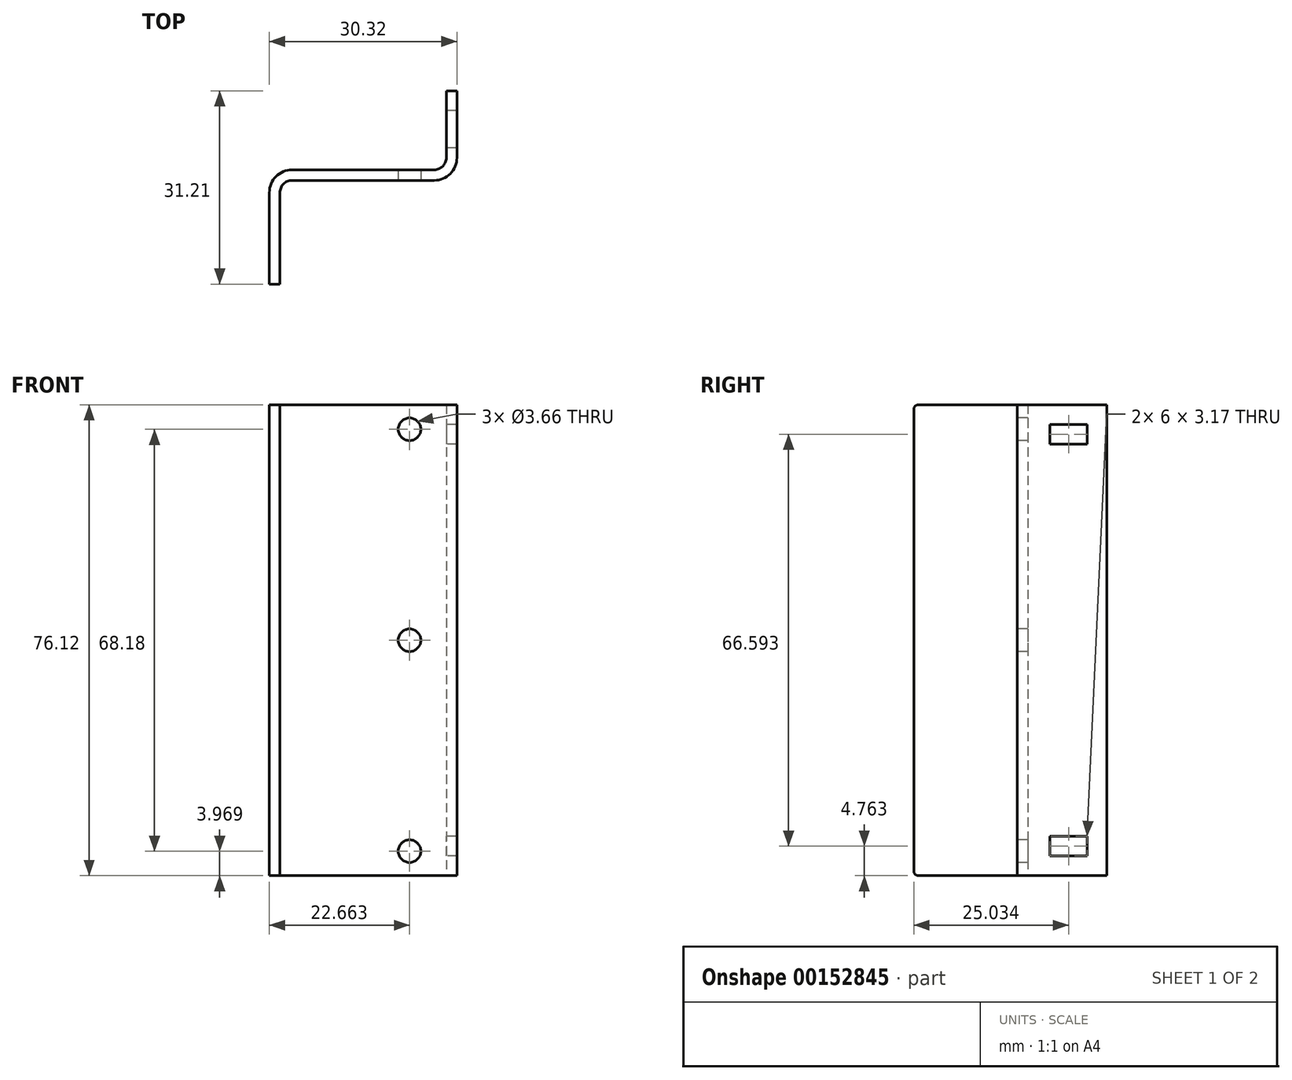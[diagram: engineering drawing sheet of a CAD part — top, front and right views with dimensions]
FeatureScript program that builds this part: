
annotation { "Feature Type Name" : "Feature", "Feature Type Description" : "" }
export const myFeature = defineFeature(function(context is Context, id is Id, definition is map)
    precondition{}
    {
        {
            var Q0;
            Q0=qCreatedBy(makeId("Top.planeOp"),FACE);
            var sketch = newSketch(context, id + "F0", { "sketchPlane" : qUnion([Q0])});
            skLineSegment(sketch, "E0.bottom", {"start": v(0, 0) * mm, "end": v(-1.7, 0) * mm});
            skLineSegment(sketch, "E1.left", {"start": v(0, 0) * mm, "end": v(0, 16.75) * mm});
            skLineSegment(sketch, "E1.right", {"start": v(-1.7, 0) * mm, "end": v(-1.7, 18.46) * mm});
            skLineSegment(sketch, "E2.bottom", {"start": v(0, 16.75) * mm, "end": v(28.61, 16.75) * mm});
            skLineSegment(sketch, "E2.top", {"start": v(-1.7, 18.46) * mm, "end": v(26.9, 18.46) * mm});
            skLineSegment(sketch, "E3", {"start": v(0, 16.75) * mm, "end": v(-1.7, 16.75) * mm, "construction": true});
            skLineSegment(sketch, "E4", {"start": v(0, 16.75) * mm, "end": v(0, 18.46) * mm, "construction": true});
            skLineSegment(sketch, "E5", {"start": v(28.61, 16.75) * mm, "end": v(28.61, 31.2) * mm});
            skLineSegment(sketch, "E6", {"start": v(28.61, 31.2) * mm, "end": v(26.9, 31.2) * mm});
            skLineSegment(sketch, "E7", {"start": v(26.9, 31.2) * mm, "end": v(26.9, 18.46) * mm});
            skSolve(sketch);
        }
        {
            var Q0;
            Q0=qSketchRegion(id+"F0",true);
            extrude(context, id + "F1", {"entities" : qUnion([Q0]), "depth" : 76.12 * mm});
        }
        {
            var Q0;
            Q0=makeQuery(id+"F1.opExtrude","SWEPT_EDGE",EDGE,{"disambiguationData":[OSD([sQuery(id+"F0.wireOp",EDGE,"E1.left"),sQuery(id+"F0.wireOp",EDGE,"E2.bottom")])]});
            var Q1;
            Q1=makeQuery(id+"F1.opExtrude","SWEPT_EDGE",EDGE,{"disambiguationData":[OSD([sQuery(id+"F0.wireOp",EDGE,"E1.left"),sQuery(id+"F0.wireOp",EDGE,"E2.bottom")])]});
            var Q2;
            Q2=makeQuery(id+"F1.opExtrude","SWEPT_EDGE",EDGE,{"disambiguationData":[OSD([sQuery(id+"F0.wireOp",EDGE,"E2.top"),sQuery(id+"F0.wireOp",EDGE,"E7")])]});
            fillet(context, id + "F2", {"entities" : qUnion([Q0, Q1, Q2]), "radius" : 1.98 * mm, "tangentPropagation" : true, "allowEdgeOverflow" : false});
        }
        {
            var Q0;
            Q0=makeQuery(id+"F1.opExtrude","SWEPT_EDGE",EDGE,{"disambiguationData":[OSD([sQuery(id+"F0.wireOp",EDGE,"E1.right"),sQuery(id+"F0.wireOp",EDGE,"E2.top")])]});
            var Q1;
            Q1=makeQuery(id+"F1.opExtrude","SWEPT_EDGE",EDGE,{"disambiguationData":[OSD([sQuery(id+"F0.wireOp",EDGE,"E1.right"),sQuery(id+"F0.wireOp",EDGE,"E2.top")])]});
            var Q2;
            Q2=makeQuery(id+"F1.opExtrude","SWEPT_EDGE",EDGE,{"disambiguationData":[OSD([sQuery(id+"F0.wireOp",EDGE,"E2.bottom"),sQuery(id+"F0.wireOp",EDGE,"E5")])]});
            fillet(context, id + "F3", {"entities" : qUnion([Q0, Q1, Q2]), "radius" : 3.7 * mm, "tangentPropagation" : true, "allowEdgeOverflow" : false});
        }
        {
            var Q0;
            Q0=makeQuery(id+"F1.opExtrude","SWEPT_FACE",FACE,{"disambiguationData":[OSD([sQuery(id+"F0.wireOp",EDGE,"E2.bottom")])]});
            var sketch = newSketch(context, id + "F4", { "sketchPlane" : qUnion([Q0])});
            skLineSegment(sketch, "E8", {"start": v(20.95, 76.12) * mm, "end": v(20.95, 72.15) * mm, "construction": true});
            skLineSegment(sketch, "E9", {"start": v(20.95, 72.15) * mm, "end": v(20.95, 3.97) * mm, "construction": true});
            skLineSegment(sketch, "E10", {"start": v(20.95, 3.97) * mm, "end": v(20.95, 0) * mm, "construction": true});
            skLineSegment(sketch, "E11", {"start": v(20.95, 38.06) * mm, "end": v(24.92, 38.06) * mm, "construction": true});
            skCircle(sketch, "E12", {"center": v(20.95, 72.15) * mm, "radius": 1.83 * mm});
            skCircle(sketch, "E13", {"center": v(20.95, 38.06) * mm, "radius": 1.83 * mm});
            skCircle(sketch, "E14", {"center": v(20.95, 3.97) * mm, "radius": 1.83 * mm});
            skSolve(sketch);
        }
        {
            var Q0;
            Q0 = qSketchRegion(id + "F4", true);
            var Q1;
            Q1=makeQuery(id+"F1.opExtrude","SWEPT_FACE",FACE,{"disambiguationData":[OSD([sQuery(id+"F0.wireOp",EDGE,"E2.top")])]});
            extrude(context, id + "F5", {"entities" : qUnion([Q0]), "operationType" : NewBodyOperationType.REMOVE, "endBound" : BoundingType.UP_TO_SURFACE, "oppositeDirection" : true, "endBoundEntityFace" : qUnion([Q1]), "depth" : 25.4 * mm});
        }
        {
            var Q0;
            Q0=makeQuery(id+"F1.opExtrude","CAP_EDGE",EDGE,{"disambiguationData":[OSD([sQuery(id+"F0.wireOp",EDGE,"CBXVxerA-JZwe-1R4C-h2t0-RdQutqAmHxP0")])],"isStart":false});
            var Q1;
            Q1=makeQuery(id+"F1.opExtrude","CAP_EDGE",EDGE,{"disambiguationData":[OSD([sQuery(id+"F0.wireOp",EDGE,"E0.bottom")])],"isStart":false});
            var Q2;
            Q2=makeQuery(id+"F1.opExtrude","CAP_EDGE",EDGE,{"disambiguationData":[OSD([sQuery(id+"F0.wireOp",EDGE,"E0.bottom")])],"isStart":true});
            var Q3;
            Q3=makeQuery(id+"F1.opExtrude","CAP_EDGE",EDGE,{"disambiguationData":[OSD([sQuery(id+"F0.wireOp",EDGE,"CBXVxerA-JZwe-1R4C-h2t0-RdQutqAmHxP0")])],"isStart":true});
            fillet(context, id + "F6", {"entities" : qUnion([Q0, Q1, Q2, Q3]), "radius" : 0.76 * mm, "tangentPropagation" : true, "allowEdgeOverflow" : false});
        }
        {
            var Q0;
            Q0=makeQuery(id+"F1.opExtrude","SWEPT_FACE",FACE,{"disambiguationData":[OSD([sQuery(id+"F0.wireOp",EDGE,"E7")])]});
            var sketch = newSketch(context, id + "F7", { "sketchPlane" : qUnion([Q0])});
            skLineSegment(sketch, "E15.bottom", {"start": v(-22.03, 72.94) * mm, "end": v(-28.03, 72.94) * mm});
            skLineSegment(sketch, "E15.top", {"start": v(-22.03, 69.77) * mm, "end": v(-28.03, 69.77) * mm});
            skLineSegment(sketch, "E15.left", {"start": v(-22.03, 72.94) * mm, "end": v(-22.03, 69.77) * mm});
            skLineSegment(sketch, "E15.right", {"start": v(-28.03, 72.94) * mm, "end": v(-28.03, 69.77) * mm});
            skLineSegment(sketch, "E16.bottom", {"start": v(-22.03, 3.18) * mm, "end": v(-28.03, 3.18) * mm});
            skLineSegment(sketch, "E16.top", {"start": v(-22.03, 6.35) * mm, "end": v(-28.03, 6.35) * mm});
            skLineSegment(sketch, "E16.left", {"start": v(-22.03, 3.18) * mm, "end": v(-22.03, 6.35) * mm});
            skLineSegment(sketch, "E16.right", {"start": v(-28.03, 3.18) * mm, "end": v(-28.03, 6.35) * mm});
            skLineSegment(sketch, "E17", {"start": v(-28.03, 72.94) * mm, "end": v(-31.2, 72.94) * mm, "construction": true});
            skLineSegment(sketch, "E18", {"start": v(-28.03, 72.94) * mm, "end": v(-28.03, 76.12) * mm, "construction": true});
            skLineSegment(sketch, "E19", {"start": v(-28.03, 3.18) * mm, "end": v(-31.2, 3.18) * mm, "construction": true});
            skLineSegment(sketch, "E20", {"start": v(-28.03, 3.18) * mm, "end": v(-28.03, 0) * mm, "construction": true});
            skSolve(sketch);
        }
        {
            var Q0;
            Q0 = qSketchRegion(id + "F7", true);
            var Q1;
            Q1=makeQuery(id+"F1.opExtrude","SWEPT_FACE",FACE,{"disambiguationData":[OSD([sQuery(id+"F0.wireOp",EDGE,"E5")])]});
            extrude(context, id + "F8", {"entities" : qUnion([Q0]), "operationType" : NewBodyOperationType.REMOVE, "endBound" : BoundingType.UP_TO_SURFACE, "oppositeDirection" : true, "endBoundEntityFace" : qUnion([Q1]), "depth" : 25.4 * mm});
        }
    });
